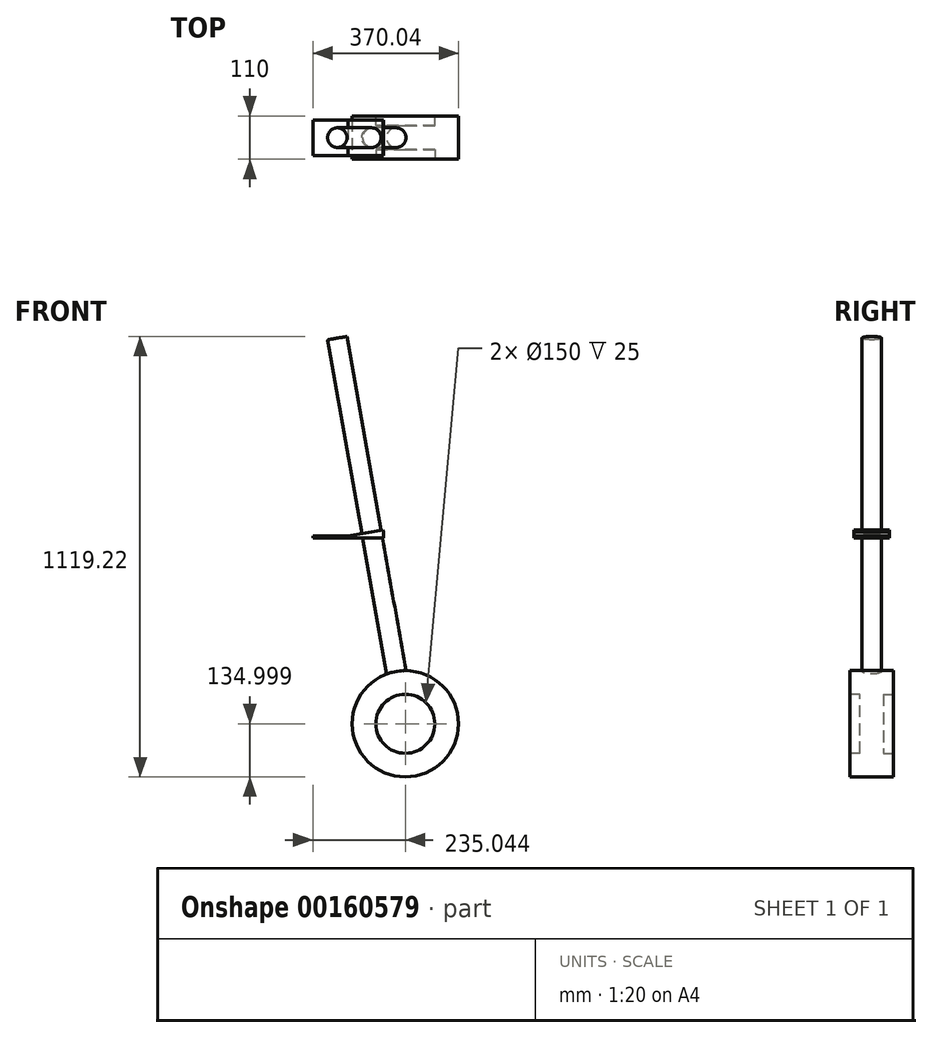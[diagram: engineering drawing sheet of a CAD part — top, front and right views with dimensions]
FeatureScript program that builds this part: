
annotation { "Feature Type Name" : "Feature", "Feature Type Description" : "" }
export const myFeature = defineFeature(function(context is Context, id is Id, definition is map)
    precondition{}
    {
        {
            var Q0;
            Q0=qCreatedBy(makeId("Top.planeOp"),FACE);
            var sketch = newSketch(context, id + "F0", { "sketchPlane" : qUnion([Q0])});
            skLineSegment(sketch, "E0.bottom", {"start": v(90, -45) * mm, "end": v(-90, -45) * mm});
            skLineSegment(sketch, "E0.top", {"start": v(90, 45) * mm, "end": v(-90, 45) * mm});
            skLineSegment(sketch, "E0.left", {"start": v(90, -45) * mm, "end": v(90, 45) * mm});
            skLineSegment(sketch, "E0.right", {"start": v(-90, -45) * mm, "end": v(-90, 45) * mm});
            skPoint(sketch, "E0.middle", {"position": v(0, 0) * mm});
            skSolve(sketch);
        }
        {
            var Q0;
            Q0=makeQuery(id+"F0.imprint","IMPRINT",FACE,{"disambiguationData":[TD([[makeQuery(id+"F0.imprint","IMPRINT",EDGE,{"derivedFrom":sQuery(id+"F0.wireOp",EDGE,"E0.bottom")}),-1.0]])]});
            extrude(context, id + "F1", {"entities" : qUnion([Q0]), "depth" : 5 * mm});
        }
        {
            var Q0;
            Q0=makeQuery(id+"F1.opExtrude","SWEPT_FACE",FACE,{"disambiguationData":[OSD([sQuery(id+"F0.wireOp",EDGE,"E0.bottom")])]});
            var sketch = newSketch(context, id + "F2", { "sketchPlane" : qUnion([Q0])});
            skLineSegment(sketch, "E1", {"start": v(0, 0) * mm, "end": v(0, 5) * mm});
            skLineSegment(sketch, "E2", {"start": v(0, 5) * mm, "end": v(88.63, 20.63) * mm});
            skLineSegment(sketch, "E3", {"start": v(88.63, 20.63) * mm, "end": v(89.5, 15.7) * mm});
            skLineSegment(sketch, "E4", {"start": v(89.5, 15.7) * mm, "end": v(0, 0) * mm});
            skLineSegment(sketch, "E5", {"start": v(90, 5) * mm, "end": v(89.5, 15.7) * mm});
            skSolve(sketch);
        }
        {
            var Q0;
            {var subQ0=sQuery(id+"F2.wireOp",EDGE,"E2");Q0=makeQuery(id+"F2.imprint","IMPRINT",FACE,{"disambiguationData":[TD([[makeQuery(id+"F2.imprint","IMPRINT",EDGE,{"derivedFrom":subQ0}),-1.0]])]});}
            var Q1;
            {var subQ0=sQuery(id+"F2.wireOp",EDGE,"E5");Q1=makeQuery(id+"F2.imprint","IMPRINT",FACE,{"disambiguationData":[TD([[makeQuery(id+"F2.imprint","IMPRINT",EDGE,{"derivedFrom":subQ0}),1.0]])]});}
            extrude(context, id + "F3", {"entities" : qUnion([Q0, Q1]), "operationType" : NewBodyOperationType.ADD, "oppositeDirection" : true, "depth" : 90 * mm});
        }
        {
            var Q0;
            Q0=makeQuery(id+"F3.opExtrude","SWEPT_FACE",FACE,{"disambiguationData":[OSD([sQuery(id+"F2.wireOp",EDGE,"E2")])]});
            var sketch = newSketch(context, id + "F4", { "sketchPlane" : qUnion([Q0])});
            skLineSegment(sketch, "E6", {"start": v(90.87, 0) * mm, "end": v(60.87, 0) * mm, "construction": true});
            skPoint(sketch, "E6.endSnap0", {"position": v(90.87, 0) * mm});
            skCircle(sketch, "E7", {"center": v(60.87, 0) * mm, "radius": 25 * mm});
            skSolve(sketch);
        }
        {
            var Q0;
            Q0=makeQuery(id+"F4.imprint","IMPRINT",FACE,{"disambiguationData":[TD([[makeQuery(id+"F4.imprint","IMPRINT",EDGE,{"derivedFrom":sQuery(id+"F4.wireOp",EDGE,"E7")}),1.0]])]});
            extrude(context, id + "F5", {"entities" : qUnion([Q0]), "operationType" : NewBodyOperationType.ADD, "oppositeDirection" : true, "depth" : 495 * mm});
        }
        {
            var Q0;
            Q0 = qSketchRegion(id + "F4", true);
            extrude(context, id + "F6", {"entities" : qUnion([Q0]), "operationType" : NewBodyOperationType.ADD, "depth" : 500 * mm});
        }
        {
            var Q0;
            Q0=makeQuery(id+"F5.opExtrude","CAP_FACE",FACE,{"disambiguationData":[OSD([sQuery(id+"F4.wireOp",EDGE,"E7")])],"isStart":false});
            var sketch = newSketch(context, id + "F7", { "sketchPlane" : qUnion([Q0])});
            skLineSegment(sketch, "E8", {"start": v(85.87, 0) * mm, "end": v(85.87, -60) * mm});
            skLineSegment(sketch, "E9", {"start": v(85.87, -60) * mm, "end": v(60.87, -60) * mm});
            skLineSegment(sketch, "E10", {"start": v(85.87, 0) * mm, "end": v(85.87, 60) * mm});
            skLineSegment(sketch, "E11", {"start": v(85.87, 60) * mm, "end": v(60.87, 60) * mm});
            skLineSegment(sketch, "E12", {"start": v(35.87, 0) * mm, "end": v(35.87, 60) * mm});
            skLineSegment(sketch, "E13", {"start": v(35.87, 60) * mm, "end": v(60.87, 60) * mm});
            skLineSegment(sketch, "E14", {"start": v(35.87, 0) * mm, "end": v(35.87, -60) * mm});
            skLineSegment(sketch, "E15", {"start": v(35.87, -60) * mm, "end": v(60.87, -60) * mm});
            skLineSegment(sketch, "E16", {"start": v(85.87, 0) * mm, "end": v(35.87, 0) * mm});
            skLineSegment(sketch, "E17", {"start": v(60.87, 60) * mm, "end": v(60.87, -60) * mm});
            skSolve(sketch);
        }
        {
            var Q0;
            Q0=sQuery(id+"F7.wireOp",EDGE,"E17");
            cPlane(context, id + "F8", {"entities" : qUnion([Q0]), "cplaneType" : CPlaneType.MID_PLANE, "offset" : 25 * mm, "width" : 150 * mm, "height" : 150 * mm});
        }
        {
            var Q0;
            Q0=qCreatedBy(id+"F8.planeOp",FACE);
            var sketch = newSketch(context, id + "F9", { "sketchPlane" : qUnion([Q0])});
            skLineSegment(sketch, "E18.0", {"start": v(-169.66, -467.72) * mm, "end": v(-120.42, -476.4) * mm});
            skCircle(sketch, "E19", {"center": v(-145.04, -472.06) * mm, "radius": 135 * mm});
            skSolve(sketch);
        }
        {
            var Q0;
            Q0=makeQuery(id+"F9.imprint","IMPRINT",FACE,{"disambiguationData":[TD([[makeQuery(id+"F9.imprint","IMPRINT",EDGE,{"derivedFrom":sQuery(id+"F9.wireOp",EDGE,"E19")}),1.0]])]});
            extrude(context, id + "F10", {"entities" : qUnion([Q0]), "operationType" : NewBodyOperationType.ADD, "depth" : 110 * mm, "symmetric" : true});
        }
        {
            var Q0;
            Q0=makeQuery(id+"F10.opExtrude","CAP_FACE",FACE,{"disambiguationData":[OSD([sQuery(id+"F9.wireOp",EDGE,"E19")])],"isStart":true});
            var sketch = newSketch(context, id + "F11", { "sketchPlane" : qUnion([Q0])});
            skCircle(sketch, "E20", {"center": v(145.04, -472.06) * mm, "radius": 75 * mm});
            skSolve(sketch);
        }
        {
            var Q0;
            Q0=makeQuery(id+"F11.imprint","IMPRINT",FACE,{"disambiguationData":[TD([[makeQuery(id+"F11.imprint","IMPRINT",EDGE,{"derivedFrom":sQuery(id+"F11.wireOp",EDGE,"E20")}),1.0]])]});
            extrude(context, id + "F12", {"entities" : qUnion([Q0]), "operationType" : NewBodyOperationType.REMOVE, "oppositeDirection" : true, "depth" : 25 * mm});
        }
        {
            var Q0;
            Q0=makeQuery(id+"F10.opExtrude","CAP_FACE",FACE,{"disambiguationData":[OSD([sQuery(id+"F9.wireOp",EDGE,"E19")])],"isStart":false});
            var sketch = newSketch(context, id + "F13", { "sketchPlane" : qUnion([Q0])});
            skCircle(sketch, "E21", {"center": v(-145.04, -472.06) * mm, "radius": 75 * mm});
            skSolve(sketch);
        }
        {
            var Q0;
            Q0=makeQuery(id+"F13.imprint","IMPRINT",FACE,{"disambiguationData":[TD([[makeQuery(id+"F13.imprint","IMPRINT",EDGE,{"derivedFrom":sQuery(id+"F13.wireOp",EDGE,"E21")}),1.0]])]});
            extrude(context, id + "F14", {"entities" : qUnion([Q0]), "operationType" : NewBodyOperationType.REMOVE, "oppositeDirection" : true, "depth" : 25 * mm});
        }
    });
